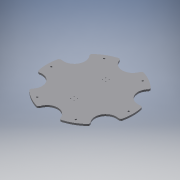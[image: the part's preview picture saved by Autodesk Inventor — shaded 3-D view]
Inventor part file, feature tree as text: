
AUTODESK INVENTOR PART (.ipt)
format: ipt  version: 2019 (Build 230136000, 136)  size: 224,768 bytes
history: native  units: mm
features: extrude x5, sketch x5, other x3, hole x3, pattern_circular x1, fillet x1
ambient origin geometry x8: Origin, YZ Plane, XZ Plane, XY Plane, X Axis, Y Axis, Z Axis, Center Point
bodies: Body1 (feature_tree)
feature tree (18):
  other  "крепление2"
  other  "Твердое тело1"
  extrude  "Выдавливание8"  Depth=4.0mm
  hole  "Отверстие2"  [1 undecoded]
  hole  "Отверстие3"  [1 undecoded]
  extrude  "Выдавливание9"  Depth=4.0mm
  pattern_circular  "Круговой массив1"  [2 undecoded]
  fillet  "Сопряжение1"  Radius=4.0mm
  extrude  "Выдавливание1"  Depth=4.0mm
  extrude  "Выдавливание4"  Depth=4.0mm
  extrude  "Выдавливание5"  Depth=9.0mm
  hole  "Отверстие1"  [1 undecoded]
  sketch  "Эскиз6"
  sketch  "Эскиз7"
  other  "Твердое тело2"
  sketch  "Эскиз8"
  sketch  "Эскиз9"
  sketch  "Эскиз10"
note: 5 required parameter values undecoded (feature->parameter linkage not recoverable at this tier; creation-order binding heuristic only, values carry confidence <= 0.55)
